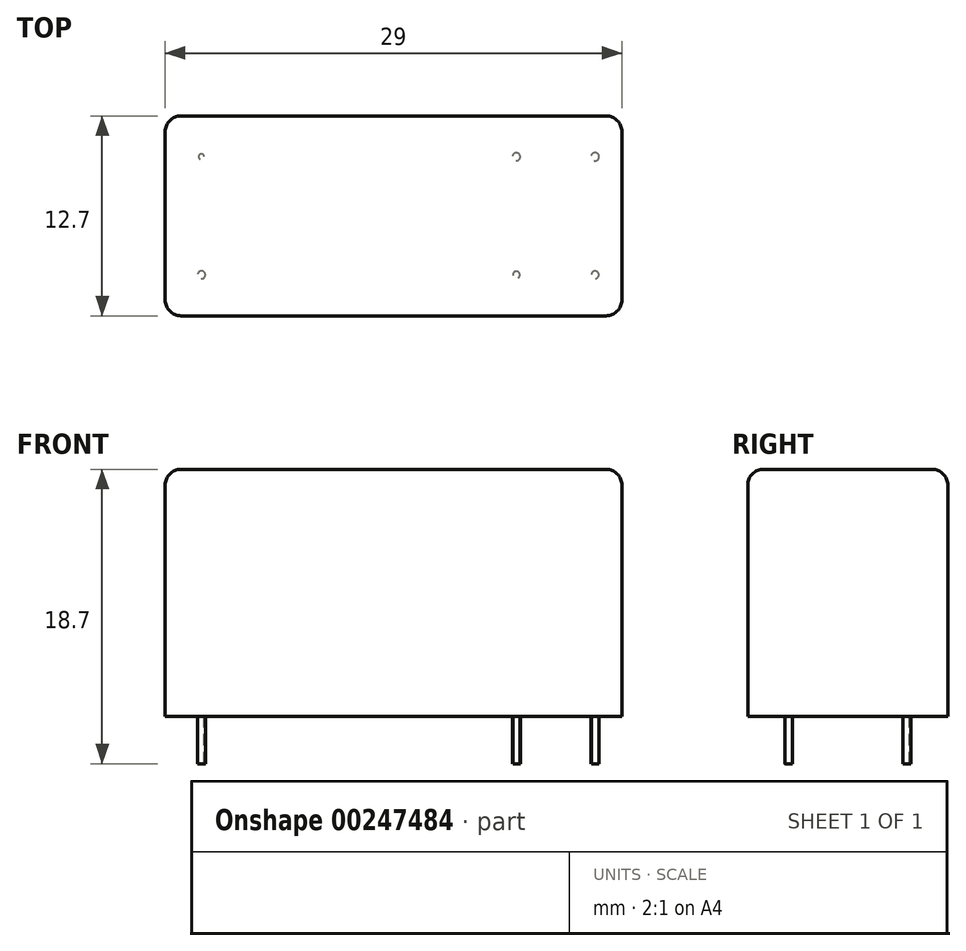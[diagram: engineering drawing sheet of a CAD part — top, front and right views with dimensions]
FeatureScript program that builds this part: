
annotation { "Feature Type Name" : "Feature", "Feature Type Description" : "" }
export const myFeature = defineFeature(function(context is Context, id is Id, definition is map)
    precondition{}
    {
        {
            var Q0;
            Q0=qCreatedBy(makeId("Top.planeOp"),FACE);
            var sketch = newSketch(context, id + "F0", { "sketchPlane" : qUnion([Q0])});
            skLineSegment(sketch, "E0.rect.bottom", {"start": v(14.5, -6.35) * mm, "end": v(-14.5, -6.35) * mm});
            skLineSegment(sketch, "E0.rect.top", {"start": v(14.5, 6.35) * mm, "end": v(-14.5, 6.35) * mm});
            skLineSegment(sketch, "E0.rect.left", {"start": v(14.5, -6.35) * mm, "end": v(14.5, 6.35) * mm});
            skLineSegment(sketch, "E0.rect.right", {"start": v(-14.5, -6.35) * mm, "end": v(-14.5, 6.35) * mm});
            skPoint(sketch, "E0.rect.middle", {"position": v(0, 0) * mm});
            skSolve(sketch);
        }
        {
            var Q0;
            Q0=makeQuery(id+"F0.imprint","IMPRINT",FACE,{"disambiguationData":[TD([[makeQuery(id+"F0.imprint","IMPRINT",EDGE,{"derivedFrom":sQuery(id+"F0.wireOp",EDGE,"E0.rect.bottom")}),-1.0]])]});
            extrude(context, id + "F1", {"entities" : qUnion([Q0]), "depth" : 15.7 * mm});
        }
        {
            var Q0;
            Q0=makeQuery(id+"F1.opExtrude","CAP_FACE",FACE,{"disambiguationData":[OSD([sQuery(id+"F0.wireOp",EDGE,"E0.rect.bottom"),sQuery(id+"F0.wireOp",EDGE,"E0.rect.top"),sQuery(id+"F0.wireOp",EDGE,"E0.rect.left"),sQuery(id+"F0.wireOp",EDGE,"E0.rect.right")])],"isStart":true});
            var sketch = newSketch(context, id + "F2", { "sketchPlane" : qUnion([Q0])});
            skCircle(sketch, "E1", {"center": v(-12.2, 3.75) * mm, "radius": 0.25 * mm});
            skCircle(sketch, "E2", {"center": v(-12.2, -3.75) * mm, "radius": 0.18 * mm});
            skCircle(sketch, "E3", {"center": v(7.8, 3.75) * mm, "radius": 0.22 * mm});
            skCircle(sketch, "E4", {"center": v(12.8, 3.75) * mm, "radius": 0.24 * mm});
            skCircle(sketch, "E5", {"center": v(7.8, -3.75) * mm, "radius": 0.25 * mm});
            skCircle(sketch, "E6", {"center": v(12.8, -3.75) * mm, "radius": 0.26 * mm});
            skLineSegment(sketch, "E7", {"start": v(-14.5, 0) * mm, "end": v(14.5, 0) * mm, "construction": true});
            skSolve(sketch);
        }
        {
            var Q0;
            Q0=qSketchRegion(id+"F2",true);
            extrude(context, id + "F3", {"entities" : qUnion([Q0]), "depth" : 3 * mm});
        }
        {
            var Q0;
            Q0=makeQuery(id+"F1.opExtrude","CAP_EDGE",EDGE,{"disambiguationData":[OSD([sQuery(id+"F0.wireOp",EDGE,"E0.rect.bottom")])],"isStart":false});
            var Q1;
            Q1=makeQuery(id+"F1.opExtrude","CAP_EDGE",EDGE,{"disambiguationData":[OSD([sQuery(id+"F0.wireOp",EDGE,"E0.rect.right")])],"isStart":false});
            var Q2;
            Q2=makeQuery(id+"F1.opExtrude","CAP_EDGE",EDGE,{"disambiguationData":[OSD([sQuery(id+"F0.wireOp",EDGE,"E0.rect.top")])],"isStart":false});
            var Q3;
            Q3=makeQuery(id+"F1.opExtrude","CAP_EDGE",EDGE,{"disambiguationData":[OSD([sQuery(id+"F0.wireOp",EDGE,"E0.rect.left")])],"isStart":false});
            var Q4;
            Q4=makeQuery(id+"F1.opExtrude","SWEPT_EDGE",EDGE,{"disambiguationData":[OSD([sQuery(id+"F0.wireOp",EDGE,"E0.rect.bottom"),sQuery(id+"F0.wireOp",EDGE,"E0.rect.left")])]});
            var Q5;
            Q5=makeQuery(id+"F1.opExtrude","SWEPT_EDGE",EDGE,{"disambiguationData":[OSD([sQuery(id+"F0.wireOp",EDGE,"E0.rect.top"),sQuery(id+"F0.wireOp",EDGE,"E0.rect.left")])]});
            var Q6;
            Q6=makeQuery(id+"F1.opExtrude","SWEPT_EDGE",EDGE,{"disambiguationData":[OSD([sQuery(id+"F0.wireOp",EDGE,"E0.rect.bottom"),sQuery(id+"F0.wireOp",EDGE,"E0.rect.right")])]});
            var Q7;
            Q7=makeQuery(id+"F1.opExtrude","SWEPT_EDGE",EDGE,{"disambiguationData":[OSD([sQuery(id+"F0.wireOp",EDGE,"E0.rect.top"),sQuery(id+"F0.wireOp",EDGE,"E0.rect.right")])]});
            fillet(context, id + "F4", {"entities" : qUnion([Q0, Q1, Q2, Q3, Q4, Q5, Q6, Q7]), "radius" : 1 * mm, "tangentPropagation" : true, "allowEdgeOverflow" : false});
        }
    });
